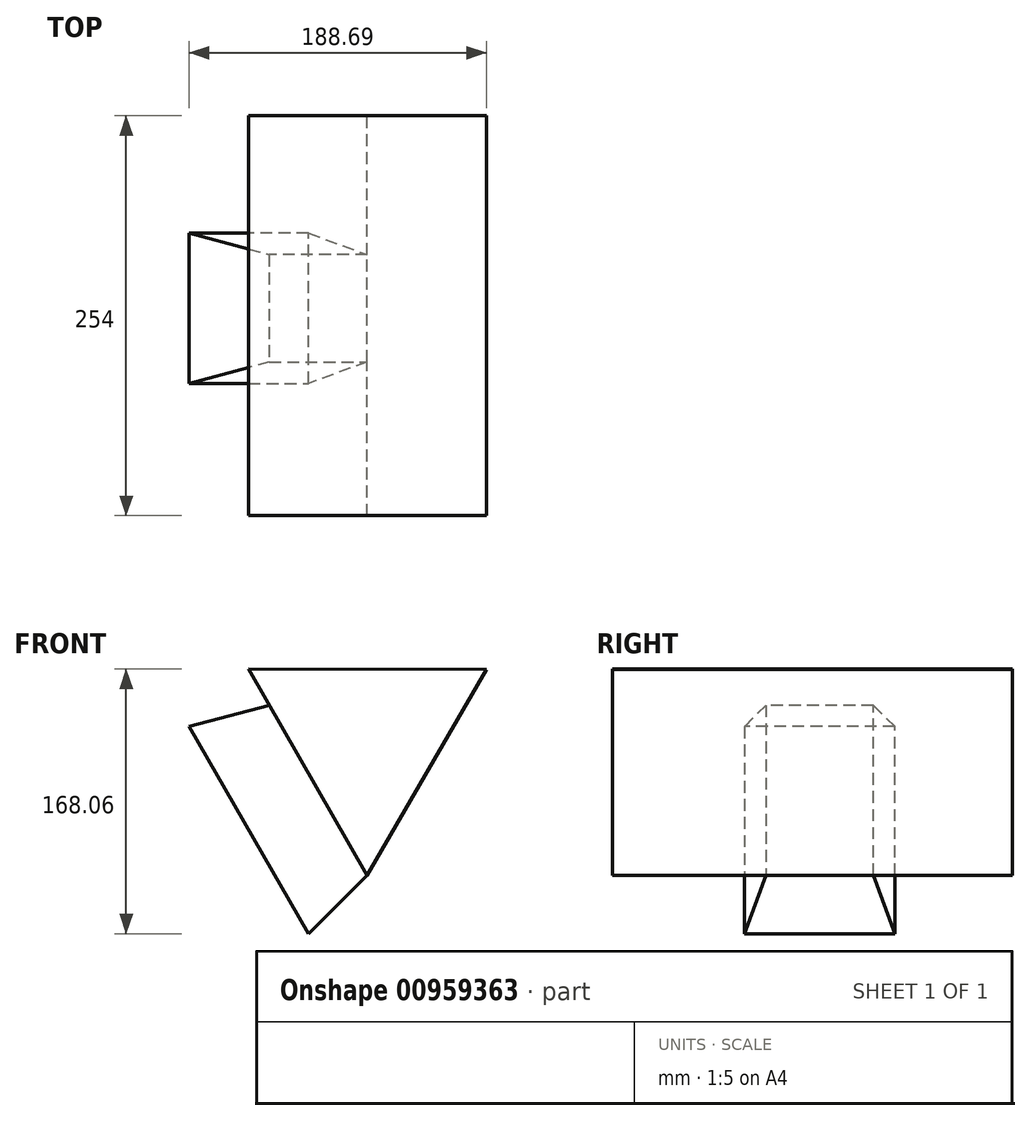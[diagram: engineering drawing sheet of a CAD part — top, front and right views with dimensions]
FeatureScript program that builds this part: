
annotation { "Feature Type Name" : "Feature", "Feature Type Description" : "" }
export const myFeature = defineFeature(function(context is Context, id is Id, definition is map)
    precondition{}
    {
        {
            var Q0;
            Q0=qCreatedBy(makeId("Front.planeOp"),FACE);
            var sketch = newSketch(context, id + "F0", { "sketchPlane" : qUnion([Q0])});
            skCircle(sketch, "E0.cCircle", {"center": v(0, 0) * mm, "radius": 43.6 * mm, "construction": true});
            skLineSegment(sketch, "E0.0", {"start": v(75.6, 43.5) * mm, "end": v(-0.13, -87.21) * mm});
            skLineSegment(sketch, "E0.1", {"start": v(-0.13, -87.21) * mm, "end": v(-75.46, 43.72) * mm});
            skLineSegment(sketch, "E0.2", {"start": v(-75.46, 43.72) * mm, "end": v(75.6, 43.5) * mm});
            skPoint(sketch, "E0.0.midPoint", {"position": v(37.73, -21.86) * mm});
            skSolve(sketch);
        }
        {
            var Q0;
            Q0 = qSketchRegion(id + "F0", true);
            extrude(context, id + "F1", {"entities" : qUnion([Q0]), "depth" : 254 * mm, "offsetDistance" : 25.4 * mm});
        }
        {
            var Q0;
            Q0=makeQuery(id+"F1.opExtrude","SWEPT_FACE",FACE,{"disambiguationData":[OSD([sQuery(id+"F0.wireOp",EDGE,"E0.1")])]});
            var sketch = newSketch(context, id + "F2", { "sketchPlane" : qUnion([Q0])});
            skLineSegment(sketch, "E1.bottom", {"start": v(88.22, -75.53) * mm, "end": v(156.36, -75.53) * mm});
            skLineSegment(sketch, "E1.top", {"start": v(88.22, 49.07) * mm, "end": v(156.36, 49.07) * mm});
            skLineSegment(sketch, "E1.left", {"start": v(88.22, -75.53) * mm, "end": v(88.22, 49.07) * mm});
            skLineSegment(sketch, "E1.right", {"start": v(156.36, -75.53) * mm, "end": v(156.36, 49.07) * mm});
            skSolve(sketch);
        }
        {
            var Q0;
            Q0=makeQuery(id+"F2.imprint","IMPRINT",FACE,{"disambiguationData":[TD([[makeQuery(id+"F2.imprint","IMPRINT",EDGE,{"derivedFrom":sQuery(id+"F2.wireOp",EDGE,"E1.bottom")}),-1.0]])]});
            extrude(context, id + "F3", {"entities" : qUnion([Q0]), "operationType" : NewBodyOperationType.ADD, "depth" : 50.8 * mm, "offsetDistance" : 25.4 * mm, "hasDraft" : true, "draftAngle" : 15 * degree});
        }
    });
